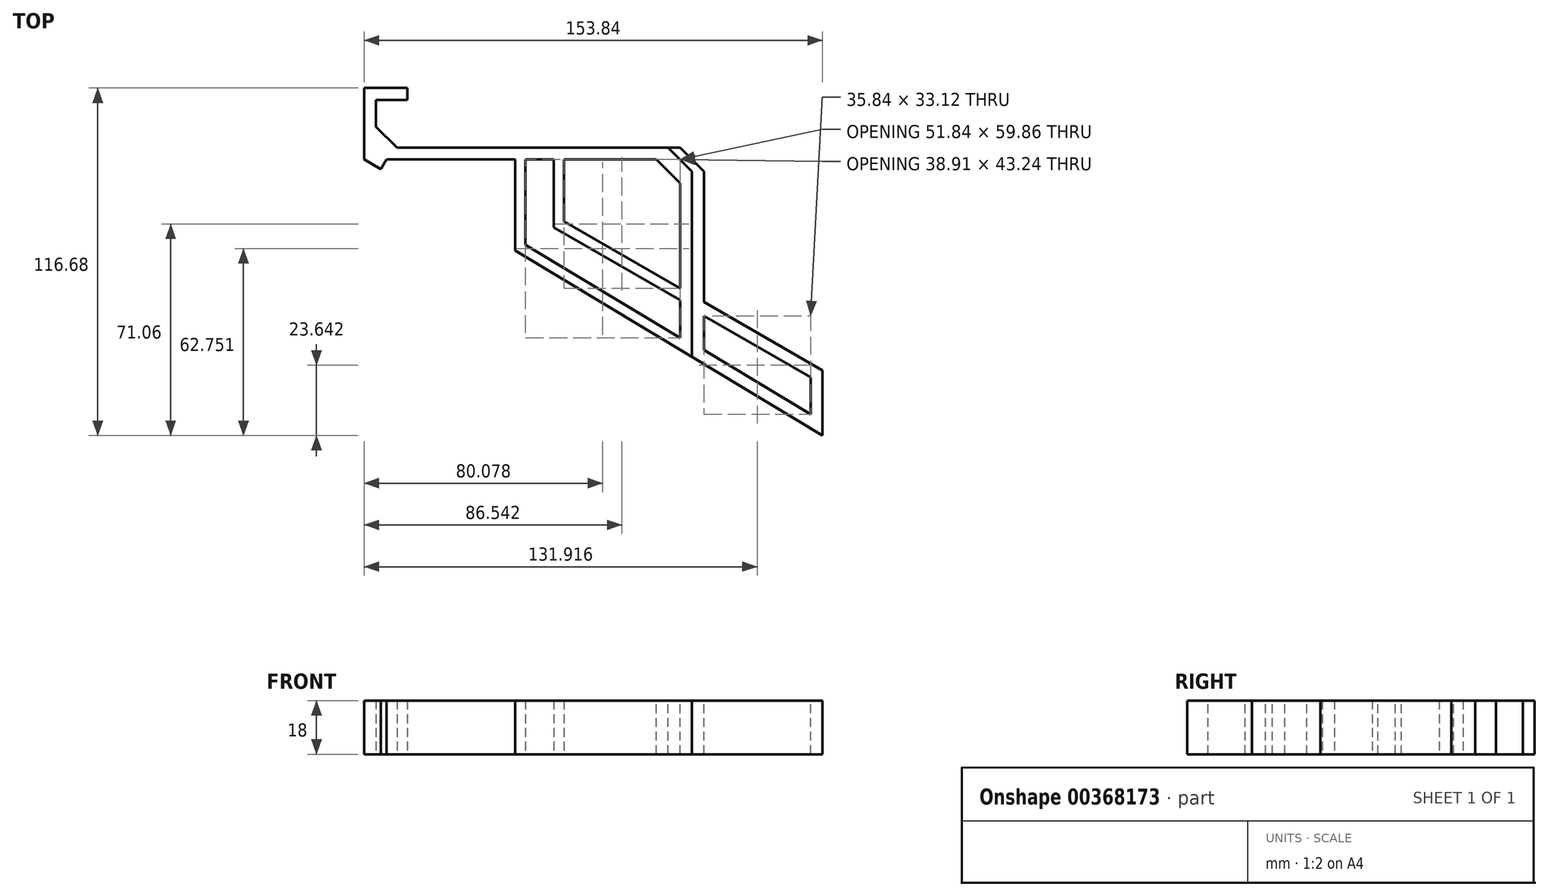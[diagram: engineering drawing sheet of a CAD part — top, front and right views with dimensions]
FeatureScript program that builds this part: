
annotation { "Feature Type Name" : "Feature", "Feature Type Description" : "" }
export const myFeature = defineFeature(function(context is Context, id is Id, definition is map)
    precondition{}
    {
        {
            var Q0;
            Q0=qCreatedBy(makeId("Top.planeOp"),FACE);
            var sketch = newSketch(context, id + "F0", { "sketchPlane" : qUnion([Q0])});
            skLineSegment(sketch, "E0", {"start": v(0, 16) * mm, "end": v(-10.43, 16) * mm});
            skLineSegment(sketch, "E1", {"start": v(-10.43, 16) * mm, "end": v(-10.43, 0) * mm});
            skLineSegment(sketch, "E2", {"start": v(-10.43, 0) * mm, "end": v(95.57, 0) * mm});
            skLineSegment(sketch, "E3.0", {"start": v(-14.43, -4) * mm, "end": v(95.57, -4) * mm});
            skLineSegment(sketch, "E3.1", {"start": v(-14.43, 20) * mm, "end": v(-14.43, -4) * mm});
            skLineSegment(sketch, "E3.2", {"start": v(0, 20) * mm, "end": v(-14.43, 20) * mm});
            skLineSegment(sketch, "E4", {"start": v(0, 16) * mm, "end": v(0, 20) * mm});
            skLineSegment(sketch, "E5", {"start": v(95.57, 0) * mm, "end": v(95.57, -4) * mm});
            skLineSegment(sketch, "E6", {"start": v(-10.43, 7) * mm, "end": v(-3.43, 0) * mm});
            skLineSegment(sketch, "E7", {"start": v(95.57, -4) * mm, "end": v(95.57, -70.27) * mm});
            skLineSegment(sketch, "E8", {"start": v(95.57, -70.27) * mm, "end": v(91.57, -67.86) * mm});
            skLineSegment(sketch, "E9", {"start": v(91.57, -67.86) * mm, "end": v(91.57, -4) * mm});
            skLineSegment(sketch, "E10", {"start": v(-14.43, -4) * mm, "end": v(95.57, -70.27) * mm, "construction": true});
            skSolve(sketch);
        }
        {
            var Q0;
            Q0 = qSketchRegion(id + "F0", true);
            extrude(context, id + "F1", {"entities" : qUnion([Q0]), "depth" : 18 * mm, "symmetric" : true});
        }
        {
            var Q0;
            Q0=makeQuery(id+"F1.opExtrude","CAP_FACE",FACE,{"disambiguationData":[OSD([sQuery(id+"F0.wireOp",EDGE,"E0"),sQuery(id+"F0.wireOp",EDGE,"E1"),sQuery(id+"F0.wireOp",EDGE,"E2"),sQuery(id+"F0.wireOp",EDGE,"E3.0"),sQuery(id+"F0.wireOp",EDGE,"E3.1"),sQuery(id+"F0.wireOp",EDGE,"E3.2"),sQuery(id+"F0.wireOp",EDGE,"E4"),sQuery(id+"F0.wireOp",EDGE,"E5"),sQuery(id+"F0.wireOp",EDGE,"E6"),sQuery(id+"F0.wireOp",EDGE,"E7"),sQuery(id+"F0.wireOp",EDGE,"E8"),sQuery(id+"F0.wireOp",EDGE,"E9")])],"isStart":false});
            var sketch = newSketch(context, id + "F2", { "sketchPlane" : qUnion([Q0])});
            skLineSegment(sketch, "E11", {"start": v(95.57, -70.27) * mm, "end": v(-14.43, -4) * mm});
            skLineSegment(sketch, "E12", {"start": v(-14.43, -4) * mm, "end": v(-43.04, -4) * mm});
            skLineSegment(sketch, "E13", {"start": v(-43.04, -4) * mm, "end": v(-43.04, -70.27) * mm});
            skLineSegment(sketch, "E14", {"start": v(-43.04, -70.27) * mm, "end": v(95.57, -70.27) * mm});
            skSolve(sketch);
        }
        {
            var Q0;
            Q0 = qSketchRegion(id + "F2", true);
            extrude(context, id + "F3", {"entities" : qUnion([Q0]), "operationType" : NewBodyOperationType.REMOVE, "oppositeDirection" : true, "depth" : 25 * mm});
        }
        {
            var Q0;
            Q0=makeQuery(id+"F1.opExtrude","CAP_FACE",FACE,{"disambiguationData":[OSD([sQuery(id+"F0.wireOp",EDGE,"E0"),sQuery(id+"F0.wireOp",EDGE,"E1"),sQuery(id+"F0.wireOp",EDGE,"E2"),sQuery(id+"F0.wireOp",EDGE,"E3.0"),sQuery(id+"F0.wireOp",EDGE,"E3.1"),sQuery(id+"F0.wireOp",EDGE,"E3.2"),sQuery(id+"F0.wireOp",EDGE,"E4"),sQuery(id+"F0.wireOp",EDGE,"E5"),sQuery(id+"F0.wireOp",EDGE,"E6"),sQuery(id+"F0.wireOp",EDGE,"E7"),sQuery(id+"F0.wireOp",EDGE,"E8"),sQuery(id+"F0.wireOp",EDGE,"E9")])],"isStart":false});
            var sketch = newSketch(context, id + "F4", { "sketchPlane" : qUnion([Q0])});
            skCircle(sketch, "E15.cCircle", {"center": v(91.57, -4) * mm, "radius": 63.86 * mm, "construction": true});
            skLineSegment(sketch, "E15.0", {"start": v(91.57, -67.86) * mm, "end": v(36.26, -35.93) * mm});
            skLineSegment(sketch, "E15.1", {"start": v(36.26, -35.93) * mm, "end": v(36.26, 27.93) * mm});
            skLineSegment(sketch, "E15.2", {"start": v(36.26, 27.93) * mm, "end": v(91.57, 59.86) * mm});
            skLineSegment(sketch, "E15.3", {"start": v(91.57, 59.86) * mm, "end": v(146.87, 27.93) * mm});
            skLineSegment(sketch, "E15.4", {"start": v(146.87, 27.93) * mm, "end": v(146.87, -35.93) * mm});
            skLineSegment(sketch, "E15.5", {"start": v(146.87, -35.93) * mm, "end": v(91.57, -67.86) * mm});
            skCircle(sketch, "E16.cCircle", {"center": v(91.57, -4) * mm, "radius": 59.86 * mm, "construction": true});
            skLineSegment(sketch, "E16.0", {"start": v(91.57, -63.86) * mm, "end": v(39.73, -33.93) * mm});
            skLineSegment(sketch, "E16.1", {"start": v(39.73, -33.93) * mm, "end": v(39.73, 25.93) * mm});
            skLineSegment(sketch, "E16.2", {"start": v(39.73, 25.93) * mm, "end": v(91.57, 55.86) * mm});
            skLineSegment(sketch, "E16.3", {"start": v(91.57, 55.86) * mm, "end": v(143.4, 25.93) * mm});
            skLineSegment(sketch, "E16.4", {"start": v(143.4, 25.93) * mm, "end": v(143.4, -33.93) * mm});
            skLineSegment(sketch, "E16.5", {"start": v(143.4, -33.93) * mm, "end": v(91.57, -63.86) * mm});
            skSolve(sketch);
        }
        {
            var Q0;
            Q0 = qSketchRegion(id + "F4", true);
            extrude(context, id + "F5", {"entities" : qUnion([Q0]), "operationType" : NewBodyOperationType.ADD, "oppositeDirection" : true, "depth" : 18 * mm});
        }
        {
            var Q0;
            Q0=makeQuery(id+"F5.boolean.opBoolean","MERGE",FACE,{"derivedFrom":[makeQuery(id+"F1.opExtrude","CAP_FACE",FACE,{"disambiguationData":[OSD([sQuery(id+"F0.wireOp",EDGE,"E0"),sQuery(id+"F0.wireOp",EDGE,"E1"),sQuery(id+"F0.wireOp",EDGE,"E2"),sQuery(id+"F0.wireOp",EDGE,"E3.0"),sQuery(id+"F0.wireOp",EDGE,"E3.1"),sQuery(id+"F0.wireOp",EDGE,"E3.2"),sQuery(id+"F0.wireOp",EDGE,"E4"),sQuery(id+"F0.wireOp",EDGE,"E5"),sQuery(id+"F0.wireOp",EDGE,"E6"),sQuery(id+"F0.wireOp",EDGE,"E7"),sQuery(id+"F0.wireOp",EDGE,"E8"),sQuery(id+"F0.wireOp",EDGE,"E9")])],"isStart":false}),makeQuery(id+"F5.opExtrude","CAP_FACE",FACE,{"disambiguationData":[OSD([sQuery(id+"F4.wireOp",EDGE,"E15.0"),sQuery(id+"F4.wireOp",EDGE,"E15.1"),sQuery(id+"F4.wireOp",EDGE,"E15.2"),sQuery(id+"F4.wireOp",EDGE,"E15.3"),sQuery(id+"F4.wireOp",EDGE,"E15.4"),sQuery(id+"F4.wireOp",EDGE,"E15.5"),sQuery(id+"F4.wireOp",EDGE,"E16.0"),sQuery(id+"F4.wireOp",EDGE,"E16.1"),sQuery(id+"F4.wireOp",EDGE,"E16.2"),sQuery(id+"F4.wireOp",EDGE,"E16.3"),sQuery(id+"F4.wireOp",EDGE,"E16.4"),sQuery(id+"F4.wireOp",EDGE,"E16.5")])],"isStart":true})]});
            var sketch = newSketch(context, id + "F6", { "sketchPlane" : qUnion([Q0])});
            skCircle(sketch, "E17.cCircle", {"center": v(95.57, 0) * mm, "radius": 53.55 * mm, "construction": true});
            skLineSegment(sketch, "E17.0", {"start": v(95.57, -53.55) * mm, "end": v(49.2, -26.77) * mm});
            skLineSegment(sketch, "E17.1", {"start": v(49.2, -26.77) * mm, "end": v(49.2, 26.77) * mm});
            skLineSegment(sketch, "E17.2", {"start": v(49.2, 26.77) * mm, "end": v(95.57, 53.55) * mm});
            skLineSegment(sketch, "E17.3", {"start": v(95.57, 53.55) * mm, "end": v(141.94, 26.77) * mm});
            skLineSegment(sketch, "E17.4", {"start": v(141.94, 26.77) * mm, "end": v(141.94, -26.77) * mm});
            skLineSegment(sketch, "E17.5", {"start": v(141.94, -26.77) * mm, "end": v(95.57, -53.55) * mm});
            skCircle(sketch, "E18.cCircle", {"center": v(95.57, 0) * mm, "radius": 49.55 * mm, "construction": true});
            skLineSegment(sketch, "E18.0", {"start": v(95.57, -49.55) * mm, "end": v(52.66, -24.77) * mm});
            skLineSegment(sketch, "E18.1", {"start": v(52.66, -24.77) * mm, "end": v(52.66, 24.77) * mm});
            skLineSegment(sketch, "E18.2", {"start": v(52.66, 24.77) * mm, "end": v(95.57, 49.55) * mm});
            skLineSegment(sketch, "E18.3", {"start": v(95.57, 49.55) * mm, "end": v(138.48, 24.77) * mm});
            skLineSegment(sketch, "E18.4", {"start": v(138.48, 24.77) * mm, "end": v(138.48, -24.77) * mm});
            skLineSegment(sketch, "E18.5", {"start": v(138.48, -24.77) * mm, "end": v(95.57, -49.55) * mm});
            skSolve(sketch);
        }
        {
            var Q0;
            Q0 = qSketchRegion(id + "F6", true);
            extrude(context, id + "F7", {"entities" : qUnion([Q0]), "operationType" : NewBodyOperationType.ADD, "oppositeDirection" : true, "depth" : 18 * mm});
        }
        {
            var Q0;
            Q0=makeQuery(id+"F1.opExtrude","SWEPT_EDGE",EDGE,{"disambiguationData":[OSD([sQuery(id+"F0.wireOp",EDGE,"E3.0"),sQuery(id+"F0.wireOp",EDGE,"E9")])]});
            chamfer(context, id + "F8", {"entities" : qUnion([Q0]), "width" : 8 * mm, "tangentPropagation" : true});
        }
        {
            var Q0;
            Q0=makeQuery(id+"F1.opExtrude","SWEPT_EDGE",EDGE,{"disambiguationData":[OSD([sQuery(id+"F0.wireOp",EDGE,"E2"),sQuery(id+"F0.wireOp",EDGE,"E5")])]});
            chamfer(context, id + "F9", {"entities" : qUnion([Q0]), "width" : 8 * mm, "tangentPropagation" : true});
        }
        {
            var Q0;
            Q0=makeQuery(id+"F7.boolean.opBoolean","MERGE",FACE,{"derivedFrom":[makeQuery(id+"F5.boolean.opBoolean","MERGE",FACE,{"derivedFrom":[makeQuery(id+"F1.opExtrude","CAP_FACE",FACE,{"disambiguationData":[OSD([sQuery(id+"F0.wireOp",EDGE,"E0"),sQuery(id+"F0.wireOp",EDGE,"E1"),sQuery(id+"F0.wireOp",EDGE,"E2"),sQuery(id+"F0.wireOp",EDGE,"E3.0"),sQuery(id+"F0.wireOp",EDGE,"E3.1"),sQuery(id+"F0.wireOp",EDGE,"E3.2"),sQuery(id+"F0.wireOp",EDGE,"E4"),sQuery(id+"F0.wireOp",EDGE,"E5"),sQuery(id+"F0.wireOp",EDGE,"E6"),sQuery(id+"F0.wireOp",EDGE,"E7"),sQuery(id+"F0.wireOp",EDGE,"E8"),sQuery(id+"F0.wireOp",EDGE,"E9")])],"isStart":false}),makeQuery(id+"F5.opExtrude","CAP_FACE",FACE,{"disambiguationData":[OSD([sQuery(id+"F4.wireOp",EDGE,"E15.0"),sQuery(id+"F4.wireOp",EDGE,"E15.1"),sQuery(id+"F4.wireOp",EDGE,"E15.2"),sQuery(id+"F4.wireOp",EDGE,"E15.3"),sQuery(id+"F4.wireOp",EDGE,"E15.4"),sQuery(id+"F4.wireOp",EDGE,"E15.5"),sQuery(id+"F4.wireOp",EDGE,"E16.0"),sQuery(id+"F4.wireOp",EDGE,"E16.1"),sQuery(id+"F4.wireOp",EDGE,"E16.2"),sQuery(id+"F4.wireOp",EDGE,"E16.3"),sQuery(id+"F4.wireOp",EDGE,"E16.4"),sQuery(id+"F4.wireOp",EDGE,"E16.5")])],"isStart":true})]}),makeQuery(id+"F7.opExtrude","CAP_FACE",FACE,{"disambiguationData":[OSD([sQuery(id+"F6.wireOp",EDGE,"E17.0"),sQuery(id+"F6.wireOp",EDGE,"E17.1"),sQuery(id+"F6.wireOp",EDGE,"E17.2"),sQuery(id+"F6.wireOp",EDGE,"E17.3"),sQuery(id+"F6.wireOp",EDGE,"E17.4"),sQuery(id+"F6.wireOp",EDGE,"E17.5"),sQuery(id+"F6.wireOp",EDGE,"E18.0"),sQuery(id+"F6.wireOp",EDGE,"E18.1"),sQuery(id+"F6.wireOp",EDGE,"E18.2"),sQuery(id+"F6.wireOp",EDGE,"E18.3"),sQuery(id+"F6.wireOp",EDGE,"E18.4"),sQuery(id+"F6.wireOp",EDGE,"E18.5")])],"isStart":true})]});
            var sketch = newSketch(context, id + "F10", { "sketchPlane" : qUnion([Q0])});
            skLineSegment(sketch, "E19", {"start": v(28.5, 0) * mm, "end": v(95.57, 0) * mm});
            skLineSegment(sketch, "E20", {"start": v(95.57, 0) * mm, "end": v(95.57, -73.17) * mm});
            skLineSegment(sketch, "E21", {"start": v(95.57, -73.17) * mm, "end": v(150.76, -38.64) * mm});
            skLineSegment(sketch, "E22", {"start": v(150.76, -38.64) * mm, "end": v(155.26, 64.33) * mm});
            skLineSegment(sketch, "E23", {"start": v(155.26, 64.33) * mm, "end": v(108.49, 79.65) * mm});
            skLineSegment(sketch, "E24", {"start": v(108.49, 79.65) * mm, "end": v(24.9, 40.95) * mm});
            skLineSegment(sketch, "E25", {"start": v(24.9, 40.95) * mm, "end": v(28.5, 0) * mm});
            skSolve(sketch);
        }
        {
            var Q0;
            Q0 = qSketchRegion(id + "F10", true);
            extrude(context, id + "F11", {"entities" : qUnion([Q0]), "operationType" : NewBodyOperationType.REMOVE, "oppositeDirection" : true, "depth" : 25 * mm});
        }
        {
            var Q0;
            Q0=makeQuery(id+"F7.boolean.opBoolean","MERGE",FACE,{"derivedFrom":[makeQuery(id+"F5.boolean.opBoolean","MERGE",FACE,{"derivedFrom":[makeQuery(id+"F1.opExtrude","CAP_FACE",FACE,{"disambiguationData":[OSD([sQuery(id+"F0.wireOp",EDGE,"E0"),sQuery(id+"F0.wireOp",EDGE,"E1"),sQuery(id+"F0.wireOp",EDGE,"E2"),sQuery(id+"F0.wireOp",EDGE,"E3.0"),sQuery(id+"F0.wireOp",EDGE,"E3.1"),sQuery(id+"F0.wireOp",EDGE,"E3.2"),sQuery(id+"F0.wireOp",EDGE,"E4"),sQuery(id+"F0.wireOp",EDGE,"E5"),sQuery(id+"F0.wireOp",EDGE,"E6"),sQuery(id+"F0.wireOp",EDGE,"E7"),sQuery(id+"F0.wireOp",EDGE,"E8"),sQuery(id+"F0.wireOp",EDGE,"E9")])],"isStart":false}),makeQuery(id+"F5.opExtrude","CAP_FACE",FACE,{"disambiguationData":[OSD([sQuery(id+"F4.wireOp",EDGE,"E15.0"),sQuery(id+"F4.wireOp",EDGE,"E15.1"),sQuery(id+"F4.wireOp",EDGE,"E15.2"),sQuery(id+"F4.wireOp",EDGE,"E15.3"),sQuery(id+"F4.wireOp",EDGE,"E15.4"),sQuery(id+"F4.wireOp",EDGE,"E15.5"),sQuery(id+"F4.wireOp",EDGE,"E16.0"),sQuery(id+"F4.wireOp",EDGE,"E16.1"),sQuery(id+"F4.wireOp",EDGE,"E16.2"),sQuery(id+"F4.wireOp",EDGE,"E16.3"),sQuery(id+"F4.wireOp",EDGE,"E16.4"),sQuery(id+"F4.wireOp",EDGE,"E16.5")])],"isStart":true})]}),makeQuery(id+"F7.opExtrude","CAP_FACE",FACE,{"disambiguationData":[OSD([sQuery(id+"F6.wireOp",EDGE,"E17.0"),sQuery(id+"F6.wireOp",EDGE,"E17.1"),sQuery(id+"F6.wireOp",EDGE,"E17.2"),sQuery(id+"F6.wireOp",EDGE,"E17.3"),sQuery(id+"F6.wireOp",EDGE,"E17.4"),sQuery(id+"F6.wireOp",EDGE,"E17.5"),sQuery(id+"F6.wireOp",EDGE,"E18.0"),sQuery(id+"F6.wireOp",EDGE,"E18.1"),sQuery(id+"F6.wireOp",EDGE,"E18.2"),sQuery(id+"F6.wireOp",EDGE,"E18.3"),sQuery(id+"F6.wireOp",EDGE,"E18.4"),sQuery(id+"F6.wireOp",EDGE,"E18.5")])],"isStart":true})]});
            var sketch = newSketch(context, id + "F12", { "sketchPlane" : qUnion([Q0])});
            skLineSegment(sketch, "E26", {"start": v(-14.43, -4) * mm, "end": v(-8.84, -7.23) * mm});
            skLineSegment(sketch, "E27", {"start": v(-8.84, -7.23) * mm, "end": v(-6.97, -4) * mm});
            skLineSegment(sketch, "E28", {"start": v(-6.97, -4) * mm, "end": v(-14.43, -4) * mm});
            skSolve(sketch);
        }
        {
            var Q0;
            Q0 = qSketchRegion(id + "F12", true);
            extrude(context, id + "F13", {"entities" : qUnion([Q0]), "operationType" : NewBodyOperationType.ADD, "oppositeDirection" : true, "depth" : 18 * mm});
        }
        {
            var Q0;
            Q0=makeQuery(id+"F13.boolean.opBoolean","MERGE",FACE,{"derivedFrom":[makeQuery(id+"F7.boolean.opBoolean","MERGE",FACE,{"derivedFrom":[makeQuery(id+"F5.boolean.opBoolean","MERGE",FACE,{"derivedFrom":[makeQuery(id+"F1.opExtrude","CAP_FACE",FACE,{"disambiguationData":[OSD([sQuery(id+"F0.wireOp",EDGE,"E0"),sQuery(id+"F0.wireOp",EDGE,"E1"),sQuery(id+"F0.wireOp",EDGE,"E2"),sQuery(id+"F0.wireOp",EDGE,"E3.0"),sQuery(id+"F0.wireOp",EDGE,"E3.1"),sQuery(id+"F0.wireOp",EDGE,"E3.2"),sQuery(id+"F0.wireOp",EDGE,"E4"),sQuery(id+"F0.wireOp",EDGE,"E5"),sQuery(id+"F0.wireOp",EDGE,"E6"),sQuery(id+"F0.wireOp",EDGE,"E7"),sQuery(id+"F0.wireOp",EDGE,"E8"),sQuery(id+"F0.wireOp",EDGE,"E9")])],"isStart":false}),makeQuery(id+"F5.opExtrude","CAP_FACE",FACE,{"disambiguationData":[OSD([sQuery(id+"F4.wireOp",EDGE,"E15.0"),sQuery(id+"F4.wireOp",EDGE,"E15.1"),sQuery(id+"F4.wireOp",EDGE,"E15.2"),sQuery(id+"F4.wireOp",EDGE,"E15.3"),sQuery(id+"F4.wireOp",EDGE,"E15.4"),sQuery(id+"F4.wireOp",EDGE,"E15.5"),sQuery(id+"F4.wireOp",EDGE,"E16.0"),sQuery(id+"F4.wireOp",EDGE,"E16.1"),sQuery(id+"F4.wireOp",EDGE,"E16.2"),sQuery(id+"F4.wireOp",EDGE,"E16.3"),sQuery(id+"F4.wireOp",EDGE,"E16.4"),sQuery(id+"F4.wireOp",EDGE,"E16.5")])],"isStart":true})]}),makeQuery(id+"F7.opExtrude","CAP_FACE",FACE,{"disambiguationData":[OSD([sQuery(id+"F6.wireOp",EDGE,"E17.0"),sQuery(id+"F6.wireOp",EDGE,"E17.1"),sQuery(id+"F6.wireOp",EDGE,"E17.2"),sQuery(id+"F6.wireOp",EDGE,"E17.3"),sQuery(id+"F6.wireOp",EDGE,"E17.4"),sQuery(id+"F6.wireOp",EDGE,"E17.5"),sQuery(id+"F6.wireOp",EDGE,"E18.0"),sQuery(id+"F6.wireOp",EDGE,"E18.1"),sQuery(id+"F6.wireOp",EDGE,"E18.2"),sQuery(id+"F6.wireOp",EDGE,"E18.3"),sQuery(id+"F6.wireOp",EDGE,"E18.4"),sQuery(id+"F6.wireOp",EDGE,"E18.5")])],"isStart":true})]}),makeQuery(id+"F13.opExtrude","CAP_FACE",FACE,{"disambiguationData":[OSD([sQuery(id+"F12.wireOp",EDGE,"E26"),sQuery(id+"F12.wireOp",EDGE,"E27"),sQuery(id+"F12.wireOp",EDGE,"E28")])],"isStart":true})]});
            var sketch = newSketch(context, id + "F14", { "sketchPlane" : qUnion([Q0])});
            skLineSegment(sketch, "E29", {"start": v(-14.43, -4) * mm, "end": v(95.57, -70.27) * mm});
            skLineSegment(sketch, "E30", {"start": v(95.57, -70.27) * mm, "end": v(95.57, -79.24) * mm});
            skLineSegment(sketch, "E31", {"start": v(95.57, -79.24) * mm, "end": v(-31.36, -4) * mm});
            skLineSegment(sketch, "E32", {"start": v(-31.36, -4) * mm, "end": v(-14.43, -4) * mm});
            skSolve(sketch);
        }
        {
            var Q0;
            Q0 = qSketchRegion(id + "F14", true);
            extrude(context, id + "F15", {"entities" : qUnion([Q0]), "operationType" : NewBodyOperationType.REMOVE, "oppositeDirection" : true, "depth" : 25 * mm});
        }
        {
            var Q0;
            Q0=makeQuery(id+"F13.boolean.opBoolean","MERGE",FACE,{"derivedFrom":[makeQuery(id+"F7.boolean.opBoolean","MERGE",FACE,{"derivedFrom":[makeQuery(id+"F5.boolean.opBoolean","MERGE",FACE,{"derivedFrom":[makeQuery(id+"F1.opExtrude","CAP_FACE",FACE,{"disambiguationData":[OSD([sQuery(id+"F0.wireOp",EDGE,"E0"),sQuery(id+"F0.wireOp",EDGE,"E1"),sQuery(id+"F0.wireOp",EDGE,"E2"),sQuery(id+"F0.wireOp",EDGE,"E3.0"),sQuery(id+"F0.wireOp",EDGE,"E3.1"),sQuery(id+"F0.wireOp",EDGE,"E3.2"),sQuery(id+"F0.wireOp",EDGE,"E4"),sQuery(id+"F0.wireOp",EDGE,"E5"),sQuery(id+"F0.wireOp",EDGE,"E6"),sQuery(id+"F0.wireOp",EDGE,"E7"),sQuery(id+"F0.wireOp",EDGE,"E8"),sQuery(id+"F0.wireOp",EDGE,"E9")])],"isStart":false}),makeQuery(id+"F5.opExtrude","CAP_FACE",FACE,{"disambiguationData":[OSD([sQuery(id+"F4.wireOp",EDGE,"E15.0"),sQuery(id+"F4.wireOp",EDGE,"E15.1"),sQuery(id+"F4.wireOp",EDGE,"E15.2"),sQuery(id+"F4.wireOp",EDGE,"E15.3"),sQuery(id+"F4.wireOp",EDGE,"E15.4"),sQuery(id+"F4.wireOp",EDGE,"E15.5"),sQuery(id+"F4.wireOp",EDGE,"E16.0"),sQuery(id+"F4.wireOp",EDGE,"E16.1"),sQuery(id+"F4.wireOp",EDGE,"E16.2"),sQuery(id+"F4.wireOp",EDGE,"E16.3"),sQuery(id+"F4.wireOp",EDGE,"E16.4"),sQuery(id+"F4.wireOp",EDGE,"E16.5")])],"isStart":true})]}),makeQuery(id+"F7.opExtrude","CAP_FACE",FACE,{"disambiguationData":[OSD([sQuery(id+"F6.wireOp",EDGE,"E17.0"),sQuery(id+"F6.wireOp",EDGE,"E17.1"),sQuery(id+"F6.wireOp",EDGE,"E17.2"),sQuery(id+"F6.wireOp",EDGE,"E17.3"),sQuery(id+"F6.wireOp",EDGE,"E17.4"),sQuery(id+"F6.wireOp",EDGE,"E17.5"),sQuery(id+"F6.wireOp",EDGE,"E18.0"),sQuery(id+"F6.wireOp",EDGE,"E18.1"),sQuery(id+"F6.wireOp",EDGE,"E18.2"),sQuery(id+"F6.wireOp",EDGE,"E18.3"),sQuery(id+"F6.wireOp",EDGE,"E18.4"),sQuery(id+"F6.wireOp",EDGE,"E18.5")])],"isStart":true})]}),makeQuery(id+"F13.opExtrude","CAP_FACE",FACE,{"disambiguationData":[OSD([sQuery(id+"F12.wireOp",EDGE,"E26"),sQuery(id+"F12.wireOp",EDGE,"E27"),sQuery(id+"F12.wireOp",EDGE,"E28")])],"isStart":true})]});
            var sketch = newSketch(context, id + "F16", { "sketchPlane" : qUnion([Q0])});
            skLineSegment(sketch, "E33", {"start": v(91.57, -63.86) * mm, "end": v(39.73, -32.63) * mm});
            skLineSegment(sketch, "E34", {"start": v(39.73, -32.63) * mm, "end": v(36.26, -34.54) * mm});
            skLineSegment(sketch, "E35", {"start": v(36.26, -34.54) * mm, "end": v(91.57, -67.86) * mm});
            skLineSegment(sketch, "E36", {"start": v(91.57, -67.86) * mm, "end": v(91.57, -63.86) * mm});
            skSolve(sketch);
        }
        {
            var Q0;
            Q0 = qSketchRegion(id + "F16", true);
            extrude(context, id + "F17", {"entities" : qUnion([Q0]), "operationType" : NewBodyOperationType.ADD, "oppositeDirection" : true, "depth" : 18 * mm});
        }
        {
            var Q0;
            Q0=makeQuery(id+"F17.boolean.opBoolean","MERGE",FACE,{"derivedFrom":[makeQuery(id+"F13.boolean.opBoolean","MERGE",FACE,{"derivedFrom":[makeQuery(id+"F7.boolean.opBoolean","MERGE",FACE,{"derivedFrom":[makeQuery(id+"F5.boolean.opBoolean","MERGE",FACE,{"derivedFrom":[makeQuery(id+"F1.opExtrude","CAP_FACE",FACE,{"disambiguationData":[OSD([sQuery(id+"F0.wireOp",EDGE,"E0"),sQuery(id+"F0.wireOp",EDGE,"E1"),sQuery(id+"F0.wireOp",EDGE,"E2"),sQuery(id+"F0.wireOp",EDGE,"E3.0"),sQuery(id+"F0.wireOp",EDGE,"E3.1"),sQuery(id+"F0.wireOp",EDGE,"E3.2"),sQuery(id+"F0.wireOp",EDGE,"E4"),sQuery(id+"F0.wireOp",EDGE,"E5"),sQuery(id+"F0.wireOp",EDGE,"E6"),sQuery(id+"F0.wireOp",EDGE,"E7"),sQuery(id+"F0.wireOp",EDGE,"E8"),sQuery(id+"F0.wireOp",EDGE,"E9")])],"isStart":false}),makeQuery(id+"F5.opExtrude","CAP_FACE",FACE,{"disambiguationData":[OSD([sQuery(id+"F4.wireOp",EDGE,"E15.0"),sQuery(id+"F4.wireOp",EDGE,"E15.1"),sQuery(id+"F4.wireOp",EDGE,"E15.2"),sQuery(id+"F4.wireOp",EDGE,"E15.3"),sQuery(id+"F4.wireOp",EDGE,"E15.4"),sQuery(id+"F4.wireOp",EDGE,"E15.5"),sQuery(id+"F4.wireOp",EDGE,"E16.0"),sQuery(id+"F4.wireOp",EDGE,"E16.1"),sQuery(id+"F4.wireOp",EDGE,"E16.2"),sQuery(id+"F4.wireOp",EDGE,"E16.3"),sQuery(id+"F4.wireOp",EDGE,"E16.4"),sQuery(id+"F4.wireOp",EDGE,"E16.5")])],"isStart":true})]}),makeQuery(id+"F7.opExtrude","CAP_FACE",FACE,{"disambiguationData":[OSD([sQuery(id+"F6.wireOp",EDGE,"E17.0"),sQuery(id+"F6.wireOp",EDGE,"E17.1"),sQuery(id+"F6.wireOp",EDGE,"E17.2"),sQuery(id+"F6.wireOp",EDGE,"E17.3"),sQuery(id+"F6.wireOp",EDGE,"E17.4"),sQuery(id+"F6.wireOp",EDGE,"E17.5"),sQuery(id+"F6.wireOp",EDGE,"E18.0"),sQuery(id+"F6.wireOp",EDGE,"E18.1"),sQuery(id+"F6.wireOp",EDGE,"E18.2"),sQuery(id+"F6.wireOp",EDGE,"E18.3"),sQuery(id+"F6.wireOp",EDGE,"E18.4"),sQuery(id+"F6.wireOp",EDGE,"E18.5")])],"isStart":true})]}),makeQuery(id+"F13.opExtrude","CAP_FACE",FACE,{"disambiguationData":[OSD([sQuery(id+"F12.wireOp",EDGE,"E26"),sQuery(id+"F12.wireOp",EDGE,"E27"),sQuery(id+"F12.wireOp",EDGE,"E28")])],"isStart":true})]}),makeQuery(id+"F17.opExtrude","CAP_FACE",FACE,{"disambiguationData":[OSD([sQuery(id+"F16.wireOp",EDGE,"E33"),sQuery(id+"F16.wireOp",EDGE,"E34"),sQuery(id+"F16.wireOp",EDGE,"E35"),sQuery(id+"F16.wireOp",EDGE,"E36")])],"isStart":true})]});
            var sketch = newSketch(context, id + "F18", { "sketchPlane" : qUnion([Q0])});
            skLineSegment(sketch, "E37", {"start": v(95.57, -70.27) * mm, "end": v(139.4, -96.68) * mm});
            skLineSegment(sketch, "E38", {"start": v(139.4, -96.68) * mm, "end": v(139.4, -92) * mm});
            skLineSegment(sketch, "E39", {"start": v(139.4, -92) * mm, "end": v(95.57, -65.6) * mm});
            skLineSegment(sketch, "E40", {"start": v(95.57, -65.6) * mm, "end": v(95.57, -8) * mm});
            skLineSegment(sketch, "E41", {"start": v(95.57, -8) * mm, "end": v(87.57, 0) * mm});
            skLineSegment(sketch, "E42", {"start": v(87.57, 0) * mm, "end": v(91.57, 0) * mm});
            skLineSegment(sketch, "E43", {"start": v(91.57, 0) * mm, "end": v(99.57, -8) * mm});
            skLineSegment(sketch, "E44", {"start": v(99.57, -8) * mm, "end": v(99.57, -68) * mm});
            skLineSegment(sketch, "E45", {"start": v(95.57, -70.27) * mm, "end": v(95.57, -65.6) * mm});
            skLineSegment(sketch, "E46", {"start": v(95.57, -49.55) * mm, "end": v(139.4, -74.86) * mm});
            skLineSegment(sketch, "E47", {"start": v(139.4, -74.86) * mm, "end": v(139.4, -79.48) * mm});
            skLineSegment(sketch, "E48", {"start": v(139.4, -79.48) * mm, "end": v(95.57, -54.17) * mm});
            skLineSegment(sketch, "E49", {"start": v(95.57, -54.17) * mm, "end": v(95.57, -49.55) * mm});
            skLineSegment(sketch, "E50", {"start": v(75.35, -37.88) * mm, "end": v(131.48, -70.28) * mm});
            skLineSegment(sketch, "E51", {"start": v(139.4, -92) * mm, "end": v(139.4, -79.48) * mm});
            skLineSegment(sketch, "E52", {"start": v(135.4, -89.6) * mm, "end": v(135.4, -77.17) * mm});
            skSolve(sketch);
        }
        {
            var Q0;
            Q0 = qSketchRegion(id + "F18", true);
            extrude(context, id + "F19", {"entities" : qUnion([Q0]), "oppositeDirection" : true, "depth" : 18 * mm});
        }
    });
